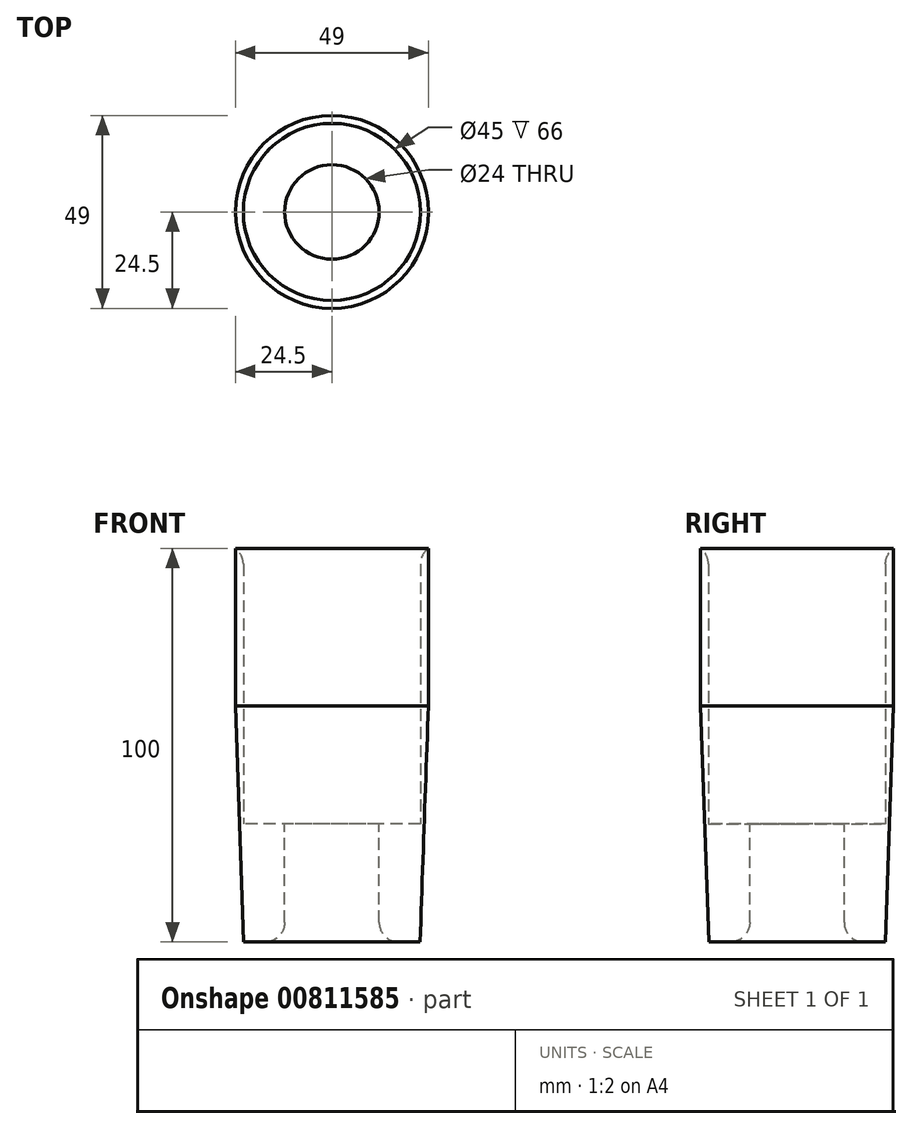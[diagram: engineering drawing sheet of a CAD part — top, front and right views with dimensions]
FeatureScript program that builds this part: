
annotation { "Feature Type Name" : "Feature", "Feature Type Description" : "" }
export const myFeature = defineFeature(function(context is Context, id is Id, definition is map)
    precondition{}
    {
        {
            var Q0;
            Q0=qCreatedBy(makeId("Top.planeOp"),FACE);
            var sketch = newSketch(context, id + "F0", { "sketchPlane" : qUnion([Q0])});
            skCircle(sketch, "E0", {"center": v(0, 0) * mm, "radius": 24.5 * mm});
            skSolve(sketch);
        }
        {
            var Q0;
            Q0 = qSketchRegion(id + "F0", true);
            extrude(context, id + "F1", {"entities" : qUnion([Q0]), "depth" : 70 * mm, "offsetDistance" : 25 * mm, "hasSecondDirection" : true, "secondDirectionOppositeDirection" : true, "secondDirectionDepth" : 30 * mm});
        }
        {
            var Q0;
            Q0=qCreatedBy(makeId("Top.planeOp"),FACE);
            var sketch = newSketch(context, id + "F2", { "sketchPlane" : qUnion([Q0])});
            skCircle(sketch, "E1", {"center": v(0, 0) * mm, "radius": 22.5 * mm});
            skSolve(sketch);
        }
        {
            var Q0;
            Q0 = qSketchRegion(id + "F2", true);
            extrude(context, id + "F3", {"entities" : qUnion([Q0]), "operationType" : NewBodyOperationType.REMOVE, "depth" : 81.3 * mm, "offsetDistance" : 25 * mm});
        }
        {
            var Q0;
            Q0=qCreatedBy(makeId("Top.planeOp"),FACE);
            var sketch = newSketch(context, id + "F4", { "sketchPlane" : qUnion([Q0])});
            skCircle(sketch, "E2", {"center": v(0, 0) * mm, "radius": 12 * mm});
            skSolve(sketch);
        }
        {
            var Q0;
            Q0 = qSketchRegion(id + "F4", true);
            extrude(context, id + "F5", {"entities" : qUnion([Q0]), "operationType" : NewBodyOperationType.REMOVE, "oppositeDirection" : true, "depth" : 41.2 * mm, "offsetDistance" : 25 * mm});
        }
        {
            var Q0;
            Q0=makeQuery(id+"F5.boolean.opBoolean","INTERSECT",EDGE,{"derivedFrom":[makeQuery(id+"F1.opExtrude","CAP_FACE",FACE,{"disambiguationData":[OSD([sQuery(id+"F0.wireOp",EDGE,"E0")])],"isStart":true}),makeQuery(id+"F5.opExtrude","SWEPT_FACE",FACE,{"disambiguationData":[OSD([sQuery(id+"F4.wireOp",EDGE,"E2")])]})]});
            fillet(context, id + "F6", {"entities" : qUnion([Q0]), "radius" : 5 * mm, "tangentPropagation" : true, "allowEdgeOverflow" : false});
        }
        {
            var Q0;
            Q0=makeQuery(id+"F1.opExtrude","CAP_EDGE",EDGE,{"disambiguationData":[OSD([sQuery(id+"F0.wireOp",EDGE,"E0")])],"isStart":true});
            chamfer(context, id + "F7", {"entities" : qUnion([Q0]), "chamferType" : ChamferType.OFFSET_ANGLE, "width" : 60 * mm, "oppositeDirection" : false, "angle" : 2 * degree, "tangentPropagation" : true});
        }
        {
            var Q0;
            Q0=makeQuery(id+"F3.boolean.opBoolean","INTERSECT",EDGE,{"derivedFrom":[makeQuery(id+"F1.opExtrude","CAP_FACE",FACE,{"disambiguationData":[OSD([sQuery(id+"F0.wireOp",EDGE,"E0")])],"isStart":false}),makeQuery(id+"F3.opExtrude","SWEPT_FACE",FACE,{"disambiguationData":[OSD([sQuery(id+"F2.wireOp",EDGE,"E1")])]})]});
            fillet(context, id + "F8", {"entities" : qUnion([Q0]), "radius" : 5 * mm, "tangentPropagation" : true, "allowEdgeOverflow" : false});
        }
    });
